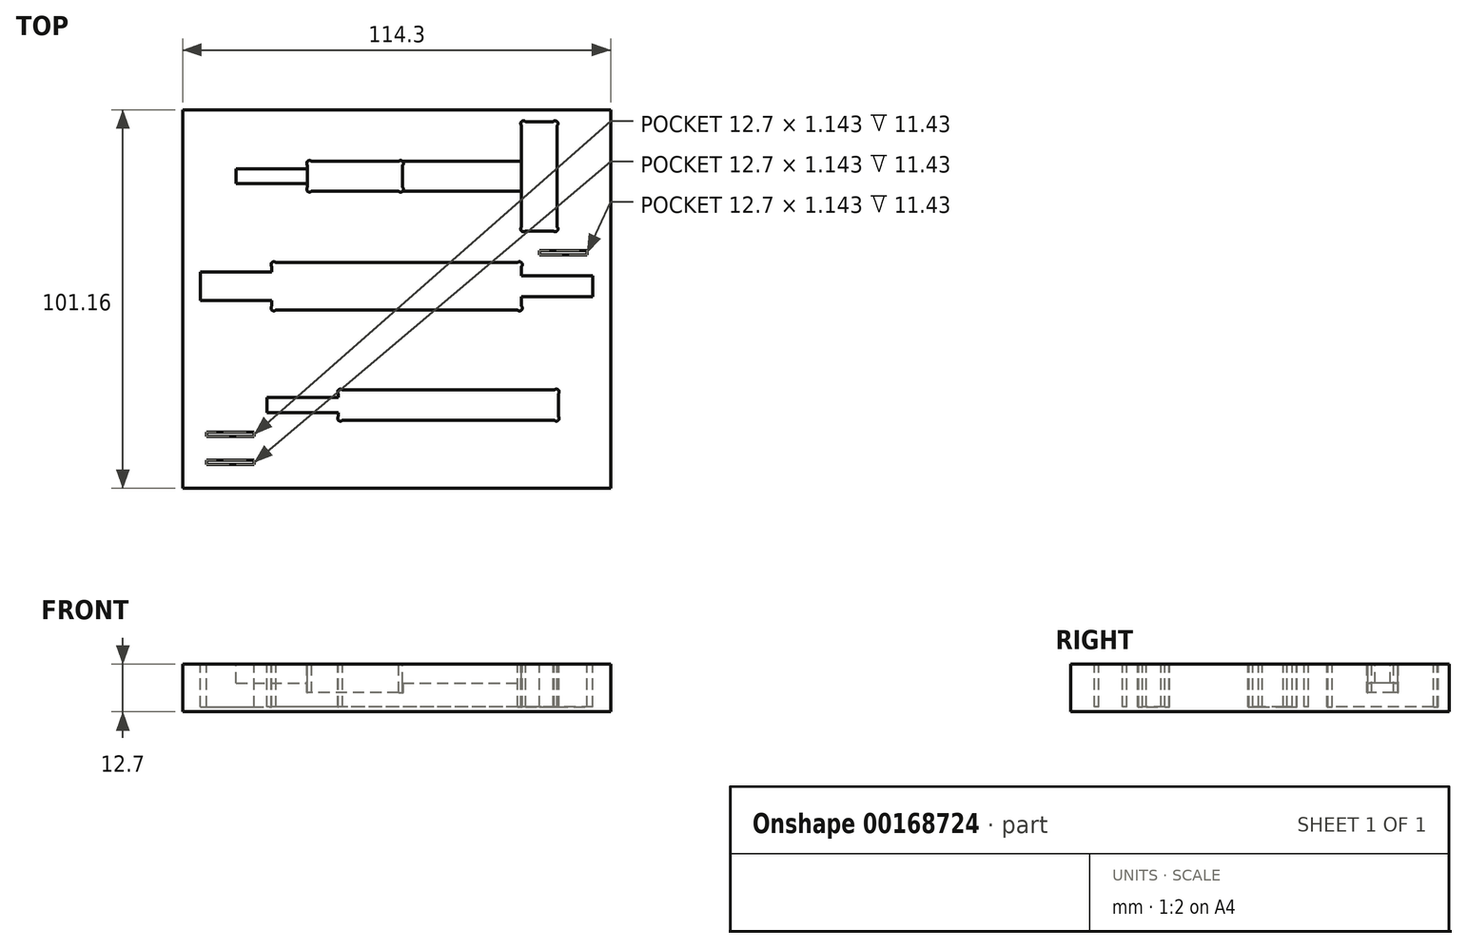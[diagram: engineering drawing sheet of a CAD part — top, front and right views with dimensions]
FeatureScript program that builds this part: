
annotation { "Feature Type Name" : "Feature", "Feature Type Description" : "" }
export const myFeature = defineFeature(function(context is Context, id is Id, definition is map)
    precondition{}
    {
        {
            var Q0;
            Q0=qCreatedBy(makeId("Top.planeOp"),FACE);
            var sketch = newSketch(context, id + "F0", { "sketchPlane" : qUnion([Q0])});
            skLineSegment(sketch, "E0.bottom", {"start": v(0, 0) * mm, "end": v(-114.3, 0) * mm});
            skLineSegment(sketch, "E0.top", {"start": v(0, -76.2) * mm, "end": v(-114.3, -76.2) * mm});
            skLineSegment(sketch, "E0.left", {"start": v(0, 0) * mm, "end": v(0, -76.2) * mm});
            skLineSegment(sketch, "E0.right", {"start": v(-114.3, 0) * mm, "end": v(-114.3, -76.2) * mm});
            skSolve(sketch);
        }
        {
            var Q0;
            Q0 = qSketchRegion(id + "F0", true);
            extrude(context, id + "F1", {"entities" : qUnion([Q0]), "depth" : 12.7 * mm});
        }
        {
            var Q0;
            Q0=makeQuery(id+"F1.opExtrude","CAP_FACE",FACE,{"disambiguationData":[OSD([sQuery(id+"F0.wireOp",EDGE,"E0.bottom"),sQuery(id+"F0.wireOp",EDGE,"E0.top"),sQuery(id+"F0.wireOp",EDGE,"E0.left"),sQuery(id+"F0.wireOp",EDGE,"E0.right")])],"isStart":false});
            var sketch = newSketch(context, id + "F2", { "sketchPlane" : qUnion([Q0])});
            skLineSegment(sketch, "E1", {"start": v(-109.54, -18.41) * mm, "end": v(-90.49, -18.41) * mm});
            skLineSegment(sketch, "E2", {"start": v(-90.49, -18.41) * mm, "end": v(-90.49, -15.88) * mm});
            skLineSegment(sketch, "E3", {"start": v(-90.49, -15.88) * mm, "end": v(-23.81, -15.88) * mm});
            skLineSegment(sketch, "E4", {"start": v(-23.81, -15.88) * mm, "end": v(-23.81, -19.43) * mm});
            skLineSegment(sketch, "E5", {"start": v(-23.81, -19.43) * mm, "end": v(-4.76, -19.43) * mm});
            skLineSegment(sketch, "E6", {"start": v(-4.76, -19.43) * mm, "end": v(-4.76, -25.02) * mm});
            skLineSegment(sketch, "E7", {"start": v(-4.76, -25.02) * mm, "end": v(-23.81, -25.02) * mm});
            skLineSegment(sketch, "E8", {"start": v(-23.81, -25.02) * mm, "end": v(-23.81, -28.58) * mm});
            skLineSegment(sketch, "E9", {"start": v(-23.81, -28.58) * mm, "end": v(-90.49, -28.58) * mm});
            skLineSegment(sketch, "E10", {"start": v(-90.49, -28.58) * mm, "end": v(-90.49, -26.04) * mm});
            skLineSegment(sketch, "E11", {"start": v(-90.49, -26.04) * mm, "end": v(-109.54, -26.04) * mm});
            skLineSegment(sketch, "E12", {"start": v(-109.54, -26.04) * mm, "end": v(-109.54, -18.41) * mm});
            skLineSegment(sketch, "E13", {"start": v(-90.49, -18.41) * mm, "end": v(-90.49, -26.04) * mm, "construction": true});
            skLineSegment(sketch, "E14", {"start": v(-23.81, -19.43) * mm, "end": v(-23.81, -25.02) * mm, "construction": true});
            skLineSegment(sketch, "E15", {"start": v(-90.49, -22.23) * mm, "end": v(-23.81, -22.23) * mm, "construction": true});
            skLineSegment(sketch, "E16", {"start": v(-57.15, -22.23) * mm, "end": v(-57.15, 0) * mm, "construction": true});
            skLineSegment(sketch, "E17", {"start": v(-109.54, -22.23) * mm, "end": v(-114.3, -22.23) * mm, "construction": true});
            skLineSegment(sketch, "E18", {"start": v(-4.76, -25.02) * mm, "end": v(0, -25.02) * mm, "construction": true});
            skSolve(sketch);
        }
        {
            var Q0;
            Q0 = qSketchRegion(id + "F2", true);
            extrude(context, id + "F3", {"entities" : qUnion([Q0]), "operationType" : NewBodyOperationType.REMOVE, "oppositeDirection" : true, "depth" : 11.43 * mm});
        }
        {
            var Q0;
            Q0=makeQuery(id+"F1.opExtrude","CAP_FACE",FACE,{"disambiguationData":[OSD([sQuery(id+"F0.wireOp",EDGE,"E0.bottom"),sQuery(id+"F0.wireOp",EDGE,"E0.top"),sQuery(id+"F0.wireOp",EDGE,"E0.left"),sQuery(id+"F0.wireOp",EDGE,"E0.right")])],"isStart":false});
            var sketch = newSketch(context, id + "F4", { "sketchPlane" : qUnion([Q0])});
            skLineSegment(sketch, "E19.bottom", {"start": v(-19.05, -12.7) * mm, "end": v(-6.35, -12.7) * mm});
            skLineSegment(sketch, "E19.top", {"start": v(-19.05, -13.84) * mm, "end": v(-6.35, -13.84) * mm});
            skLineSegment(sketch, "E19.left", {"start": v(-19.05, -12.7) * mm, "end": v(-19.05, -13.84) * mm});
            skLineSegment(sketch, "E19.right", {"start": v(-6.35, -12.7) * mm, "end": v(-6.35, -13.84) * mm});
            skLineSegment(sketch, "E20.bottom", {"start": v(-107.95, -68.7) * mm, "end": v(-95.25, -68.7) * mm});
            skLineSegment(sketch, "E20.top", {"start": v(-107.95, -69.85) * mm, "end": v(-95.25, -69.85) * mm});
            skLineSegment(sketch, "E20.left", {"start": v(-107.95, -68.7) * mm, "end": v(-107.95, -69.85) * mm});
            skLineSegment(sketch, "E20.right", {"start": v(-95.25, -68.7) * mm, "end": v(-95.25, -69.85) * mm});
            skLineSegment(sketch, "E21.bottom", {"start": v(-107.95, -61.21) * mm, "end": v(-95.25, -61.21) * mm});
            skLineSegment(sketch, "E21.top", {"start": v(-107.95, -62.36) * mm, "end": v(-95.25, -62.36) * mm});
            skLineSegment(sketch, "E21.left", {"start": v(-107.95, -61.21) * mm, "end": v(-107.95, -62.36) * mm});
            skLineSegment(sketch, "E21.right", {"start": v(-95.25, -61.21) * mm, "end": v(-95.25, -62.36) * mm});
            skSolve(sketch);
        }
        {
            var Q0;
            Q0 = qSketchRegion(id + "F4", true);
            extrude(context, id + "F5", {"entities" : qUnion([Q0]), "operationType" : NewBodyOperationType.REMOVE, "oppositeDirection" : true, "depth" : 11.43 * mm});
        }
        {
            var Q0;
            Q0=makeQuery(id+"F1.opExtrude","CAP_FACE",FACE,{"disambiguationData":[OSD([sQuery(id+"F0.wireOp",EDGE,"E0.bottom"),sQuery(id+"F0.wireOp",EDGE,"E0.top"),sQuery(id+"F0.wireOp",EDGE,"E0.left"),sQuery(id+"F0.wireOp",EDGE,"E0.right")])],"isStart":false});
            var sketch = newSketch(context, id + "F6", { "sketchPlane" : qUnion([Q0])});
            skLineSegment(sketch, "E22", {"start": v(-90.49, -18.41) * mm, "end": v(-90.49, -26.04) * mm, "construction": true});
            skLineSegment(sketch, "E23", {"start": v(-23.81, -19.43) * mm, "end": v(-23.81, -25.02) * mm, "construction": true});
            skLineSegment(sketch, "E24", {"start": v(-90.49, -22.23) * mm, "end": v(-23.81, -22.23) * mm, "construction": true});
            skCircle(sketch, "E25", {"center": v(-63.5, -22.23) * mm, "radius": 20.64 * mm, "construction": true});
            skCircle(sketch, "E26", {"center": v(-63.5, -22.23) * mm, "radius": 19.05 * mm});
            skLineSegment(sketch, "E27", {"start": v(-72.7, -53.98) * mm, "end": v(-13.97, -53.98) * mm, "construction": true});
            skCircle(sketch, "E28", {"center": v(-28.57, -53.98) * mm, "radius": 19.37 * mm});
            skCircle(sketch, "E29", {"center": v(-28.57, -53.98) * mm, "radius": 20.64 * mm, "construction": true});
            skLineSegment(sketch, "E30.bottom", {"start": v(-13.97, -49.91) * mm, "end": v(-72.7, -49.91) * mm});
            skLineSegment(sketch, "E30.top", {"start": v(-13.97, -58.04) * mm, "end": v(-72.7, -58.04) * mm});
            skLineSegment(sketch, "E30.left", {"start": v(-13.97, -49.91) * mm, "end": v(-13.97, -58.04) * mm});
            skPoint(sketch, "E30.middle", {"position": v(-43.34, -53.98) * mm});
            skLineSegment(sketch, "E31.bottom", {"start": v(-72.7, -55.97) * mm, "end": v(-91.76, -55.97) * mm});
            skLineSegment(sketch, "E31.top", {"start": v(-72.7, -51.97) * mm, "end": v(-91.76, -51.97) * mm});
            skLineSegment(sketch, "E31.right", {"start": v(-91.76, -55.97) * mm, "end": v(-91.76, -51.97) * mm});
            skLineSegment(sketch, "E32", {"start": v(-72.7, -49.91) * mm, "end": v(-72.7, -51.97) * mm});
            skLineSegment(sketch, "E33", {"start": v(-72.7, -55.97) * mm, "end": v(-72.7, -58.04) * mm});
            skLineSegment(sketch, "E34.bottom", {"start": v(-80.96, 3.18) * mm, "end": v(-23.81, 3.18) * mm});
            skLineSegment(sketch, "E34.top", {"start": v(-80.96, 11.18) * mm, "end": v(-23.81, 11.18) * mm});
            skLineSegment(sketch, "E34.right", {"start": v(-23.81, 3.18) * mm, "end": v(-23.81, 11.18) * mm, "construction": true});
            skLineSegment(sketch, "E35.bottom", {"start": v(-23.81, 21.78) * mm, "end": v(-14.29, 21.78) * mm});
            skLineSegment(sketch, "E35.top", {"start": v(-23.81, -7.43) * mm, "end": v(-14.29, -7.43) * mm});
            skLineSegment(sketch, "E35.right", {"start": v(-14.29, 21.78) * mm, "end": v(-14.29, -7.43) * mm});
            skLineSegment(sketch, "E36", {"start": v(-23.81, 21.78) * mm, "end": v(-23.81, 11.18) * mm});
            skLineSegment(sketch, "E37", {"start": v(-23.81, 3.18) * mm, "end": v(-23.81, -7.43) * mm});
            skLineSegment(sketch, "E38", {"start": v(-80.96, 11.18) * mm, "end": v(-80.96, 9.18) * mm});
            skLineSegment(sketch, "E39", {"start": v(-80.96, 9.18) * mm, "end": v(-80.96, 5.18) * mm, "construction": true});
            skLineSegment(sketch, "E40", {"start": v(-80.96, 5.18) * mm, "end": v(-80.96, 3.18) * mm});
            skLineSegment(sketch, "E41.bottom", {"start": v(-100.01, 9.18) * mm, "end": v(-80.96, 9.18) * mm});
            skLineSegment(sketch, "E41.top", {"start": v(-100.01, 5.18) * mm, "end": v(-80.96, 5.18) * mm});
            skLineSegment(sketch, "E41.left", {"start": v(-100.01, 9.18) * mm, "end": v(-100.01, 5.18) * mm});
            skLineSegment(sketch, "E42", {"start": v(-114.3, 0) * mm, "end": v(-114.3, 7.18) * mm, "construction": true});
            skLineSegment(sketch, "E43", {"start": v(-114.3, 7.18) * mm, "end": v(-100.01, 7.18) * mm, "construction": true});
            skLineSegment(sketch, "E44", {"start": v(0, 0) * mm, "end": v(0, 7.18) * mm, "construction": true});
            skLineSegment(sketch, "E45", {"start": v(0, 7.18) * mm, "end": v(-14.29, 7.18) * mm, "construction": true});
            skPoint(sketch, "E45.endSnap0", {"position": v(-14.29, 7.18) * mm});
            skLineSegment(sketch, "E46", {"start": v(-114.3, 0) * mm, "end": v(-114.3, 3.59) * mm});
            skLineSegment(sketch, "E47", {"start": v(-114.3, 0) * mm, "end": v(-114.3, 24.96) * mm});
            skLineSegment(sketch, "E48", {"start": v(-114.3, 24.96) * mm, "end": v(0, 24.96) * mm});
            skLineSegment(sketch, "E49", {"start": v(0, 24.96) * mm, "end": v(0, 0) * mm});
            skSolve(sketch);
        }
        {
            var Q0;
            Q0=makeQuery(id+"F6.imprint","IMPRINT",FACE,{"disambiguationData":[TD([[makeQuery(id+"F6.imprint","IMPRINT",EDGE,{"derivedFrom":sQuery(id+"F6.wireOp",EDGE,"E31.bottom")}),1.0]])]});
            var sketch = newSketch(context, id + "F7", { "sketchPlane" : qUnion([Q0])});
            skLineSegment(sketch, "E50.0", {"start": v(-72.7, -55.97) * mm, "end": v(-91.76, -55.97) * mm});
            skLineSegment(sketch, "E50.1", {"start": v(-72.7, -51.97) * mm, "end": v(-91.76, -51.97) * mm});
            skLineSegment(sketch, "E50.2", {"start": v(-91.76, -55.97) * mm, "end": v(-91.76, -51.97) * mm});
            skLineSegment(sketch, "E50.3", {"start": v(-13.97, -49.91) * mm, "end": v(-72.7, -49.91) * mm});
            skLineSegment(sketch, "E50.4", {"start": v(-13.97, -58.04) * mm, "end": v(-72.7, -58.04) * mm});
            skLineSegment(sketch, "E50.5", {"start": v(-72.7, -55.97) * mm, "end": v(-72.7, -58.04) * mm});
            skLineSegment(sketch, "E50.6", {"start": v(-72.7, -49.91) * mm, "end": v(-72.7, -51.97) * mm});
            skLineSegment(sketch, "E51.0", {"start": v(-13.97, -49.91) * mm, "end": v(-13.97, -58.04) * mm});
            skSolve(sketch);
        }
        {
            var Q0;
            Q0 = qSketchRegion(id + "F7", true);
            extrude(context, id + "F8", {"entities" : qUnion([Q0]), "operationType" : NewBodyOperationType.REMOVE, "oppositeDirection" : true, "depth" : 11.43 * mm});
        }
        {
            var Q0;
            Q0=makeQuery(id+"F6.imprint","IMPRINT",FACE,{"disambiguationData":[TD([[makeQuery(id+"F6.imprint","IMPRINT",EDGE,{"derivedFrom":sQuery(id+"F6.wireOp",EDGE,"E31.bottom")}),1.0]])]});
            var sketch = newSketch(context, id + "F9", { "sketchPlane" : qUnion([Q0])});
            skCircle(sketch, "E52", {"center": v(-89.96, -16.4) * mm, "radius": 0.75 * mm});
            skLineSegment(sketch, "E53", {"start": v(-90.49, -16.94) * mm, "end": v(-89.43, -15.88) * mm, "construction": true});
            skLineSegment(sketch, "E54", {"start": v(-89.96, -16.4) * mm, "end": v(-90.49, -15.87) * mm, "construction": true});
            skCircle(sketch, "E55", {"center": v(-89.96, -28.04) * mm, "radius": 0.75 * mm});
            skLineSegment(sketch, "E56", {"start": v(-89.43, -28.57) * mm, "end": v(-90.49, -27.51) * mm, "construction": true});
            skLineSegment(sketch, "E57", {"start": v(-89.96, -28.04) * mm, "end": v(-90.49, -28.58) * mm, "construction": true});
            skCircle(sketch, "E58", {"center": v(-24.34, -28.04) * mm, "radius": 0.75 * mm});
            skLineSegment(sketch, "E59", {"start": v(-23.81, -27.51) * mm, "end": v(-24.87, -28.58) * mm, "construction": true});
            skLineSegment(sketch, "E60", {"start": v(-24.34, -28.04) * mm, "end": v(-23.81, -28.58) * mm, "construction": true});
            skCircle(sketch, "E61", {"center": v(-24.34, -16.4) * mm, "radius": 0.75 * mm});
            skLineSegment(sketch, "E62", {"start": v(-24.87, -15.88) * mm, "end": v(-23.81, -16.94) * mm, "construction": true});
            skLineSegment(sketch, "E63", {"start": v(-24.34, -16.4) * mm, "end": v(-23.81, -15.87) * mm, "construction": true});
            skCircle(sketch, "E64", {"center": v(-14.5, -50.44) * mm, "radius": 0.75 * mm});
            skLineSegment(sketch, "E65", {"start": v(-15.03, -49.91) * mm, "end": v(-13.97, -50.97) * mm, "construction": true});
            skLineSegment(sketch, "E66", {"start": v(-14.5, -50.44) * mm, "end": v(-13.97, -49.91) * mm, "construction": true});
            skCircle(sketch, "E67", {"center": v(-14.5, -57.5) * mm, "radius": 0.75 * mm});
            skLineSegment(sketch, "E68", {"start": v(-13.97, -56.98) * mm, "end": v(-15.03, -58.04) * mm, "construction": true});
            skLineSegment(sketch, "E69", {"start": v(-14.5, -57.5) * mm, "end": v(-13.97, -58.04) * mm, "construction": true});
            skCircle(sketch, "E70", {"center": v(-72.18, -50.44) * mm, "radius": 0.75 * mm});
            skLineSegment(sketch, "E71", {"start": v(-72.7, -50.97) * mm, "end": v(-71.65, -49.91) * mm, "construction": true});
            skLineSegment(sketch, "E72", {"start": v(-72.18, -50.44) * mm, "end": v(-72.7, -49.91) * mm, "construction": true});
            skCircle(sketch, "E73", {"center": v(-72.18, -57.5) * mm, "radius": 0.75 * mm});
            skLineSegment(sketch, "E74", {"start": v(-71.65, -58.04) * mm, "end": v(-72.7, -56.98) * mm, "construction": true});
            skLineSegment(sketch, "E75", {"start": v(-72.18, -57.5) * mm, "end": v(-72.7, -58.04) * mm, "construction": true});
            skSolve(sketch);
        }
        {
            var Q0;
            Q0 = qSketchRegion(id + "F9", true);
            extrude(context, id + "F10", {"entities" : qUnion([Q0]), "operationType" : NewBodyOperationType.REMOVE, "oppositeDirection" : true, "depth" : 11.43 * mm});
        }
        {
            var Q0;
            Q0=makeQuery(id+"F6.imprint","IMPRINT",FACE,{"disambiguationData":[TD([[makeQuery(id+"F6.imprint","IMPRINT",EDGE,{"derivedFrom":sQuery(id+"F6.wireOp",EDGE,"E31.bottom")}),1.0]])]});
            var sketch = newSketch(context, id + "F11", { "sketchPlane" : qUnion([Q0])});
            skLineSegment(sketch, "E76.0", {"start": v(-114.3, 0) * mm, "end": v(-114.3, 24.96) * mm});
            skLineSegment(sketch, "E76.1", {"start": v(-114.3, 24.96) * mm, "end": v(0, 24.96) * mm});
            skLineSegment(sketch, "E76.2", {"start": v(0, 24.96) * mm, "end": v(0, 0) * mm});
            skLineSegment(sketch, "E76.3", {"start": v(0, 0) * mm, "end": v(-114.3, 0) * mm});
            skSolve(sketch);
        }
        {
            var Q0;
            Q0 = qSketchRegion(id + "F11", true);
            extrude(context, id + "F12", {"entities" : qUnion([Q0]), "operationType" : NewBodyOperationType.ADD, "oppositeDirection" : true, "depth" : 12.7 * mm});
        }
        {
            var Q0;
            {var subQ5=sQuery(id+"F6.wireOp",EDGE,"E34.bottom");Q0=makeQuery(id+"F6.imprint","IMPRINT",FACE,{"disambiguationData":[TD([[makeQuery(id+"F6.imprint","IMPRINT",EDGE,{"derivedFrom":subQ5}),-1.0]])]});}
            var sketch = newSketch(context, id + "F13", { "sketchPlane" : qUnion([Q0])});
            skLineSegment(sketch, "E77.7", {"start": v(-23.81, 21.78) * mm, "end": v(-23.81, 11.18) * mm});
            skLineSegment(sketch, "E77.8", {"start": v(-23.81, 21.78) * mm, "end": v(-14.29, 21.78) * mm});
            skLineSegment(sketch, "E77.9", {"start": v(-14.29, 21.78) * mm, "end": v(-14.29, -7.43) * mm});
            skLineSegment(sketch, "E77.10", {"start": v(-23.81, 3.18) * mm, "end": v(-23.81, -7.43) * mm});
            skLineSegment(sketch, "E77.11", {"start": v(-23.81, -7.43) * mm, "end": v(-14.29, -7.43) * mm});
            skLineSegment(sketch, "E78", {"start": v(-23.81, 11.18) * mm, "end": v(-23.81, 3.18) * mm});
            skSolve(sketch);
        }
        {
            var Q0;
            Q0 = qSketchRegion(id + "F13", true);
            extrude(context, id + "F14", {"entities" : qUnion([Q0]), "operationType" : NewBodyOperationType.REMOVE, "oppositeDirection" : true, "depth" : 11.43 * mm});
        }
        {
            var Q0;
            {var subQ5=sQuery(id+"F6.wireOp",EDGE,"E34.bottom");Q0=makeQuery(id+"F6.imprint","IMPRINT",FACE,{"disambiguationData":[TD([[makeQuery(id+"F6.imprint","IMPRINT",EDGE,{"derivedFrom":subQ5}),-1.0]])]});}
            var sketch = newSketch(context, id + "F15", { "sketchPlane" : qUnion([Q0])});
            skLineSegment(sketch, "E79.0", {"start": v(-80.96, 11.18) * mm, "end": v(-23.81, 11.18) * mm});
            skLineSegment(sketch, "E79.1", {"start": v(-80.96, 3.18) * mm, "end": v(-23.81, 3.18) * mm});
            skLineSegment(sketch, "E79.2", {"start": v(-100.01, 5.18) * mm, "end": v(-80.96, 5.18) * mm});
            skLineSegment(sketch, "E79.3", {"start": v(-100.01, 9.18) * mm, "end": v(-80.96, 9.18) * mm});
            skLineSegment(sketch, "E79.4", {"start": v(-100.01, 9.18) * mm, "end": v(-100.01, 5.18) * mm});
            skLineSegment(sketch, "E79.5", {"start": v(-80.96, 11.18) * mm, "end": v(-80.96, 9.18) * mm});
            skLineSegment(sketch, "E79.6", {"start": v(-80.96, 5.18) * mm, "end": v(-80.96, 3.18) * mm});
            skLineSegment(sketch, "E80", {"start": v(-23.81, 11.18) * mm, "end": v(-23.81, 3.18) * mm});
            skSolve(sketch);
        }
        {
            var Q0;
            Q0 = qSketchRegion(id + "F15", true);
            extrude(context, id + "F16", {"entities" : qUnion([Q0]), "operationType" : NewBodyOperationType.REMOVE, "oppositeDirection" : true, "depth" : 5.08 * mm});
        }
        {
            var Q0;
            Q0=makeQuery(id+"F16.boolean.opBoolean","COPY",VERTEX,{"derivedFrom":makeQuery(id+"F16.opExtrude","CAP_VERTEX",VERTEX,{"disambiguationData":[OSD([sQuery(id+"F6.wireOp",EDGE,"E36"),sQuery(id+"F15.wireOp",EDGE,"E79.0"),sQuery(id+"F15.wireOp",EDGE,"E80")])],"isStart":false})});
            var Q1;
            Q1=makeQuery(id+"F16.boolean.opBoolean","COPY",VERTEX,{"derivedFrom":makeQuery(id+"F16.opExtrude","CAP_VERTEX",VERTEX,{"disambiguationData":[OSD([sQuery(id+"F6.wireOp",EDGE,"E37"),sQuery(id+"F15.wireOp",EDGE,"E79.1"),sQuery(id+"F15.wireOp",EDGE,"E80")])],"isStart":false})});
            var Q2;
            Q2=makeQuery(id+"F16.boolean.opBoolean","COPY",VERTEX,{"derivedFrom":makeQuery(id+"F16.opExtrude","CAP_VERTEX",VERTEX,{"disambiguationData":[OSD([sQuery(id+"F15.wireOp",EDGE,"E79.3"),sQuery(id+"F15.wireOp",EDGE,"E79.4")])],"isStart":false})});
            cPlane(context, id + "F17", {"entities" : qUnion([Q0, Q1, Q2]), "cplaneType" : CPlaneType.THREE_POINT, "offset" : 25.4 * mm, "width" : 152.4 * mm, "height" : 152.4 * mm});
        }
        {
            var Q0;
            Q0=qCreatedBy(id+"F17.planeOp",FACE);
            var sketch = newSketch(context, id + "F18", { "sketchPlane" : qUnion([Q0])});
            skLineSegment(sketch, "E81", {"start": v(-55.56, 11.18) * mm, "end": v(-55.56, 3.18) * mm});
            skLineSegment(sketch, "E82", {"start": v(-55.56, 11.18) * mm, "end": v(-80.96, 11.18) * mm});
            skLineSegment(sketch, "E83", {"start": v(-80.96, 11.18) * mm, "end": v(-80.96, 3.17) * mm});
            skLineSegment(sketch, "E84", {"start": v(-80.96, 3.17) * mm, "end": v(-55.56, 3.18) * mm});
            skSolve(sketch);
        }
        {
            var Q0;
            Q0 = qSketchRegion(id + "F18", true);
            extrude(context, id + "F19", {"entities" : qUnion([Q0]), "operationType" : NewBodyOperationType.REMOVE, "oppositeDirection" : true, "depth" : 2.54 * mm});
        }
        {
            var Q0;
            {var subQ5=sQuery(id+"F6.wireOp",EDGE,"E34.bottom");Q0=makeQuery(id+"F6.imprint","IMPRINT",FACE,{"disambiguationData":[TD([[makeQuery(id+"F6.imprint","IMPRINT",EDGE,{"derivedFrom":subQ5}),-1.0]])]});}
            var sketch = newSketch(context, id + "F20", { "sketchPlane" : qUnion([Q0])});
            skCircle(sketch, "E85", {"center": v(-80.43, 10.65) * mm, "radius": 0.75 * mm});
            skLineSegment(sketch, "E86", {"start": v(-80.96, 10.12) * mm, "end": v(-79.9, 11.18) * mm, "construction": true});
            skLineSegment(sketch, "E87", {"start": v(-80.43, 10.65) * mm, "end": v(-80.96, 11.18) * mm, "construction": true});
            skCircle(sketch, "E88", {"center": v(-80.43, 3.7) * mm, "radius": 0.75 * mm});
            skLineSegment(sketch, "E89", {"start": v(-79.9, 3.18) * mm, "end": v(-80.96, 4.24) * mm, "construction": true});
            skLineSegment(sketch, "E90", {"start": v(-80.43, 3.7) * mm, "end": v(-80.96, 3.17) * mm, "construction": true});
            skCircle(sketch, "E91", {"center": v(-56.1, 10.65) * mm, "radius": 0.75 * mm});
            skLineSegment(sketch, "E92", {"start": v(-56.62, 11.18) * mm, "end": v(-55.56, 10.12) * mm, "construction": true});
            skLineSegment(sketch, "E93", {"start": v(-56.1, 10.65) * mm, "end": v(-55.56, 11.18) * mm, "construction": true});
            skCircle(sketch, "E94", {"center": v(-56.1, 3.7) * mm, "radius": 0.75 * mm});
            skLineSegment(sketch, "E95", {"start": v(-55.56, 4.24) * mm, "end": v(-56.62, 3.17) * mm, "construction": true});
            skLineSegment(sketch, "E96", {"start": v(-56.1, 3.7) * mm, "end": v(-55.56, 3.18) * mm, "construction": true});
            skCircle(sketch, "E97", {"center": v(-23.28, -6.9) * mm, "radius": 0.75 * mm});
            skLineSegment(sketch, "E98", {"start": v(-22.75, -7.43) * mm, "end": v(-23.81, -6.37) * mm, "construction": true});
            skLineSegment(sketch, "E99", {"start": v(-23.28, -6.9) * mm, "end": v(-23.81, -7.43) * mm, "construction": true});
            skCircle(sketch, "E100", {"center": v(-14.82, -6.9) * mm, "radius": 0.75 * mm});
            skLineSegment(sketch, "E101", {"start": v(-14.29, -6.37) * mm, "end": v(-15.35, -7.43) * mm, "construction": true});
            skLineSegment(sketch, "E102", {"start": v(-14.82, -6.9) * mm, "end": v(-14.29, -7.43) * mm, "construction": true});
            skCircle(sketch, "E103", {"center": v(-14.82, 21.25) * mm, "radius": 0.75 * mm});
            skLineSegment(sketch, "E104", {"start": v(-15.35, 21.78) * mm, "end": v(-14.29, 20.72) * mm, "construction": true});
            skLineSegment(sketch, "E105", {"start": v(-14.82, 21.25) * mm, "end": v(-14.29, 21.78) * mm, "construction": true});
            skCircle(sketch, "E106", {"center": v(-23.28, 21.25) * mm, "radius": 0.75 * mm});
            skLineSegment(sketch, "E107", {"start": v(-23.81, 20.72) * mm, "end": v(-22.75, 21.78) * mm, "construction": true});
            skLineSegment(sketch, "E108", {"start": v(-23.28, 21.25) * mm, "end": v(-23.81, 21.78) * mm, "construction": true});
            skSolve(sketch);
        }
        {
            var Q0;
            {var subQ0=sQuery(id+"F20.wireOp",EDGE,"E85");var subQ1=makeQuery(id+"F6.imprint","IMPRINT",EDGE,{"derivedFrom":sQuery(id+"F6.wireOp",EDGE,"E34.top")});var subQ2=makeQuery(id+"F20.imprint","INTERSECT",VERTEX,{"derivedFrom":[subQ1,subQ0]});Q0=makeQuery(id+"F20.imprint","IMPRINT",FACE,{"disambiguationData":[TD([[makeQuery(id+"F20.imprint","IMPRINT",EDGE,{"disambiguationData":[TD([[subQ2,1.0]])],"derivedFrom":subQ0}),1.0]])]});}
            var sketch = newSketch(context, id + "F21", { "sketchPlane" : qUnion([Q0])});
            skCircle(sketch, "E109.0", {"center": v(-56.1, 10.65) * mm, "radius": 0.75 * mm});
            skCircle(sketch, "E109.1", {"center": v(-56.1, 3.7) * mm, "radius": 0.75 * mm});
            skCircle(sketch, "E109.2", {"center": v(-80.43, 3.7) * mm, "radius": 0.75 * mm});
            skCircle(sketch, "E109.3", {"center": v(-80.43, 10.65) * mm, "radius": 0.75 * mm});
            skSolve(sketch);
        }
        {
            var Q0;
            Q0 = qSketchRegion(id + "F21", true);
            extrude(context, id + "F22", {"entities" : qUnion([Q0]), "operationType" : NewBodyOperationType.REMOVE, "oppositeDirection" : true, "depth" : 7.62 * mm});
        }
        {
            var Q0;
            {var subQ40=makeQuery(id+"F6.imprint","IMPRINT",EDGE,{"derivedFrom":sQuery(id+"F6.wireOp",EDGE,"E41.bottom")});Q0=makeQuery(id+"F20.imprint","IMPRINT",FACE,{"disambiguationData":[TD([[makeQuery(id+"F20.imprint","IMPRINT",EDGE,{"derivedFrom":subQ40}),1.0]])]});}
            var sketch = newSketch(context, id + "F23", { "sketchPlane" : qUnion([Q0])});
            skCircle(sketch, "E110.0", {"center": v(-23.28, -6.9) * mm, "radius": 0.75 * mm});
            skCircle(sketch, "E110.1", {"center": v(-14.82, -6.9) * mm, "radius": 0.75 * mm});
            skCircle(sketch, "E110.2", {"center": v(-23.28, 21.25) * mm, "radius": 0.75 * mm});
            skCircle(sketch, "E110.3", {"center": v(-14.82, 21.25) * mm, "radius": 0.75 * mm});
            skSolve(sketch);
        }
        {
            var Q0;
            Q0 = qSketchRegion(id + "F23", true);
            extrude(context, id + "F24", {"entities" : qUnion([Q0]), "operationType" : NewBodyOperationType.REMOVE, "oppositeDirection" : true, "depth" : 11.43 * mm});
        }
    });
